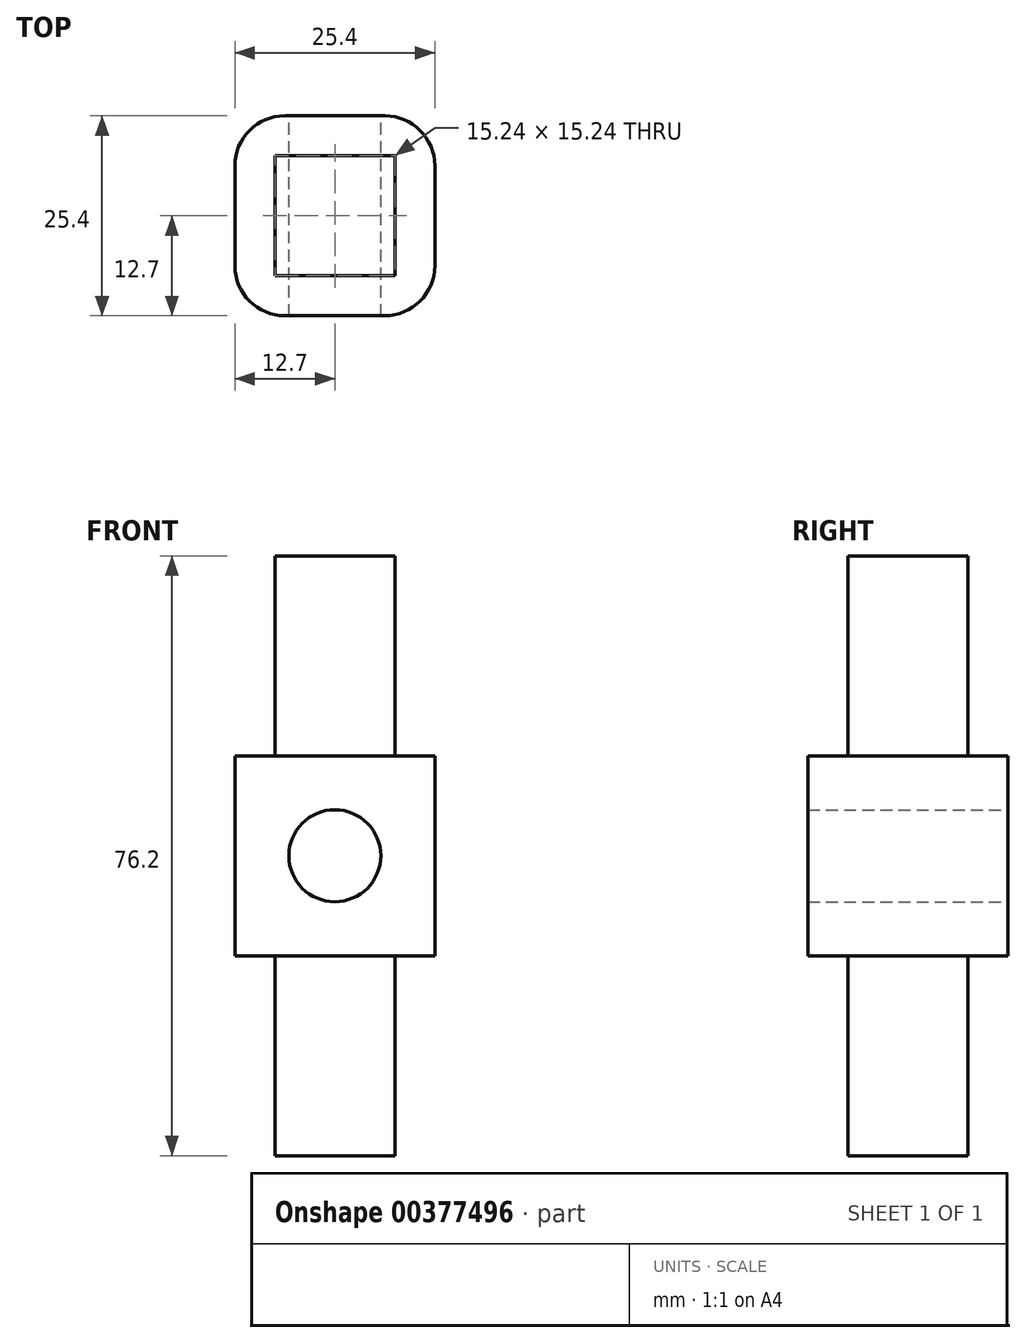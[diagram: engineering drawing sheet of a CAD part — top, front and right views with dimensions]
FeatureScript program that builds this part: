
annotation { "Feature Type Name" : "Feature", "Feature Type Description" : "" }
export const myFeature = defineFeature(function(context is Context, id is Id, definition is map)
    precondition{}
    {
        {
            var Q0;
            Q0=qCreatedBy(makeId("Front.planeOp"),FACE);
            var sketch = newSketch(context, id + "F0", { "sketchPlane" : qUnion([Q0])});
            skLineSegment(sketch, "E0", {"start": v(0, 0) * mm, "end": v(-12.7, 0) * mm});
            skLineSegment(sketch, "E1", {"start": v(-12.7, 0) * mm, "end": v(-12.7, 12.7) * mm});
            skLineSegment(sketch, "E2", {"start": v(-12.7, 12.7) * mm, "end": v(0, 12.7) * mm});
            skLineSegment(sketch, "E3.MirrorCS", {"start": v(12.7, 12.7) * mm, "end": v(0, 12.7) * mm});
            skLineSegment(sketch, "E4.MirrorCS", {"start": v(12.7, 0) * mm, "end": v(12.7, 12.7) * mm});
            skLineSegment(sketch, "E5.MirrorCS", {"start": v(0, 0) * mm, "end": v(12.7, 0) * mm});
            skSolve(sketch);
        }
        {
            var Q0;
            Q0=qSketchRegion(id+"F0",true);
            extrude(context, id + "F1", {"entities" : qUnion([Q0]), "depth" : 25.4 * mm});
        }
        {
            var Q0;
            Q0=makeQuery(id+"F1.opExtrude","SWEPT_FACE",FACE,{"disambiguationData":[OSD([sQuery(id+"F0.wireOp",EDGE,"E2"),sQuery(id+"F0.wireOp",EDGE,"E3.MirrorCS")])]});
            var sketch = newSketch(context, id + "F2", { "sketchPlane" : qUnion([Q0])});
            skLineSegment(sketch, "E6", {"start": v(0, 0) * mm, "end": v(0, -25.4) * mm});
            skLineSegment(sketch, "E7", {"start": v(0, -25.4) * mm, "end": v(0, -12.7) * mm});
            skLineSegment(sketch, "E8.bottom", {"start": v(7.62, -20.32) * mm, "end": v(-7.62, -20.32) * mm});
            skLineSegment(sketch, "E8.top", {"start": v(7.62, -5.08) * mm, "end": v(-7.62, -5.08) * mm});
            skLineSegment(sketch, "E8.left", {"start": v(7.62, -20.32) * mm, "end": v(7.62, -5.08) * mm});
            skLineSegment(sketch, "E8.right", {"start": v(-7.62, -20.32) * mm, "end": v(-7.62, -5.08) * mm});
            skPoint(sketch, "E8.middle", {"position": v(0, -12.7) * mm});
            skSolve(sketch);
        }
        {
            var Q0;
            Q0=qSketchRegion(id+"F2",true);
            extrude(context, id + "F3", {"entities" : qUnion([Q0]), "operationType" : NewBodyOperationType.ADD, "depth" : 25.4 * mm});
        }
        {
            var Q0;
            Q0=makeQuery(id+"F1.opExtrude","SWEPT_BODY",BODY,{"disambiguationData":[OSD([sQuery(id+"F0.wireOp",EDGE,"E0"),sQuery(id+"F0.wireOp",EDGE,"E1"),sQuery(id+"F0.wireOp",EDGE,"E2"),sQuery(id+"F0.wireOp",EDGE,"E3.MirrorCS"),sQuery(id+"F0.wireOp",EDGE,"E4.MirrorCS"),sQuery(id+"F0.wireOp",EDGE,"E5.MirrorCS")])]});
            var Q1;
            Q1=qCreatedBy(makeId("Top.planeOp"),FACE);
            mirror(context, id + "F4", {"operationType" : NewBodyOperationType.ADD, "entities" : qUnion([Q0]), "mirrorPlane" : qUnion([Q1])});
        }
        {
            var Q0;
            {var subQ0=makeQuery(id+"F1.opExtrude","CAP_EDGE",EDGE,{"disambiguationData":[OSD([sQuery(id+"F0.wireOp",EDGE,"E4.MirrorCS")])],"isStart":true});Q0=makeQuery(id+"F4.boolean.opBoolean","MERGE",EDGE,{"derivedFrom":[subQ0,makeQuery(id+"F4.opPattern","COPY",EDGE,{"derivedFrom":subQ0,"instanceName":"1"})]});}
            var Q1;
            {var subQ0=makeQuery(id+"F1.opExtrude","CAP_EDGE",EDGE,{"disambiguationData":[OSD([sQuery(id+"F0.wireOp",EDGE,"E4.MirrorCS")])],"isStart":false});Q1=makeQuery(id+"F4.boolean.opBoolean","MERGE",EDGE,{"derivedFrom":[subQ0,makeQuery(id+"F4.opPattern","COPY",EDGE,{"derivedFrom":subQ0,"instanceName":"1"})]});}
            var Q2;
            {var subQ0=makeQuery(id+"F1.opExtrude","CAP_EDGE",EDGE,{"disambiguationData":[OSD([sQuery(id+"F0.wireOp",EDGE,"E1")])],"isStart":true});Q2=makeQuery(id+"F4.boolean.opBoolean","MERGE",EDGE,{"derivedFrom":[subQ0,makeQuery(id+"F4.opPattern","COPY",EDGE,{"derivedFrom":subQ0,"instanceName":"1"})]});}
            var Q3;
            {var subQ0=makeQuery(id+"F1.opExtrude","CAP_EDGE",EDGE,{"disambiguationData":[OSD([sQuery(id+"F0.wireOp",EDGE,"E1")])],"isStart":false});Q3=makeQuery(id+"F4.boolean.opBoolean","MERGE",EDGE,{"derivedFrom":[subQ0,makeQuery(id+"F4.opPattern","COPY",EDGE,{"derivedFrom":subQ0,"instanceName":"1"})]});}
            fillet(context, id + "F5", {"entities" : qUnion([Q0, Q1, Q2, Q3]), "radius" : 6.35 * mm, "tangentPropagation" : true, "allowEdgeOverflow" : false});
        }
        {
            var Q0;
            {var subQ0=makeQuery(id+"F1.opExtrude","CAP_FACE",FACE,{"disambiguationData":[OSD([sQuery(id+"F0.wireOp",EDGE,"E0"),sQuery(id+"F0.wireOp",EDGE,"E1"),sQuery(id+"F0.wireOp",EDGE,"E2"),sQuery(id+"F0.wireOp",EDGE,"E3.MirrorCS"),sQuery(id+"F0.wireOp",EDGE,"E4.MirrorCS"),sQuery(id+"F0.wireOp",EDGE,"E5.MirrorCS")])],"isStart":true});Q0=makeQuery(id+"F4.boolean.opBoolean","MERGE",FACE,{"derivedFrom":[subQ0,makeQuery(id+"F4.opPattern","COPY",FACE,{"derivedFrom":subQ0,"instanceName":"1"})]});}
            var sketch = newSketch(context, id + "F6", { "sketchPlane" : qUnion([Q0])});
            skLineSegment(sketch, "E9", {"start": v(-6.35, 0) * mm, "end": v(6.35, 0) * mm});
            skLineSegment(sketch, "E10", {"start": v(6.35, 0) * mm, "end": v(0, 0) * mm});
            skSolve(sketch);
        }
        {
            var Q0;
            Q0=sQuery(id+"F6.wireOp",VERTEX,"E10.end");
            var Q1;
            Q1=makeQuery(id+"F1.opExtrude","SWEPT_BODY",BODY,{"disambiguationData":[OSD([sQuery(id+"F0.wireOp",EDGE,"E0"),sQuery(id+"F0.wireOp",EDGE,"E1"),sQuery(id+"F0.wireOp",EDGE,"E2"),sQuery(id+"F0.wireOp",EDGE,"E3.MirrorCS"),sQuery(id+"F0.wireOp",EDGE,"E4.MirrorCS"),sQuery(id+"F0.wireOp",EDGE,"E5.MirrorCS")])]});
            hole(context, id + "F7", {"style" : HoleStyle.SIMPLE, "endStyle" : HoleEndStyle.BLIND, "holeDiameter" : 11.68 * mm, "holeDepth" : 254 * mm, "tappedDepth" : 12.7 * mm, "tapClearance" : 3, "locations" : qUnion([Q0]), "scope" : qUnion([Q1])});
        }
    });
